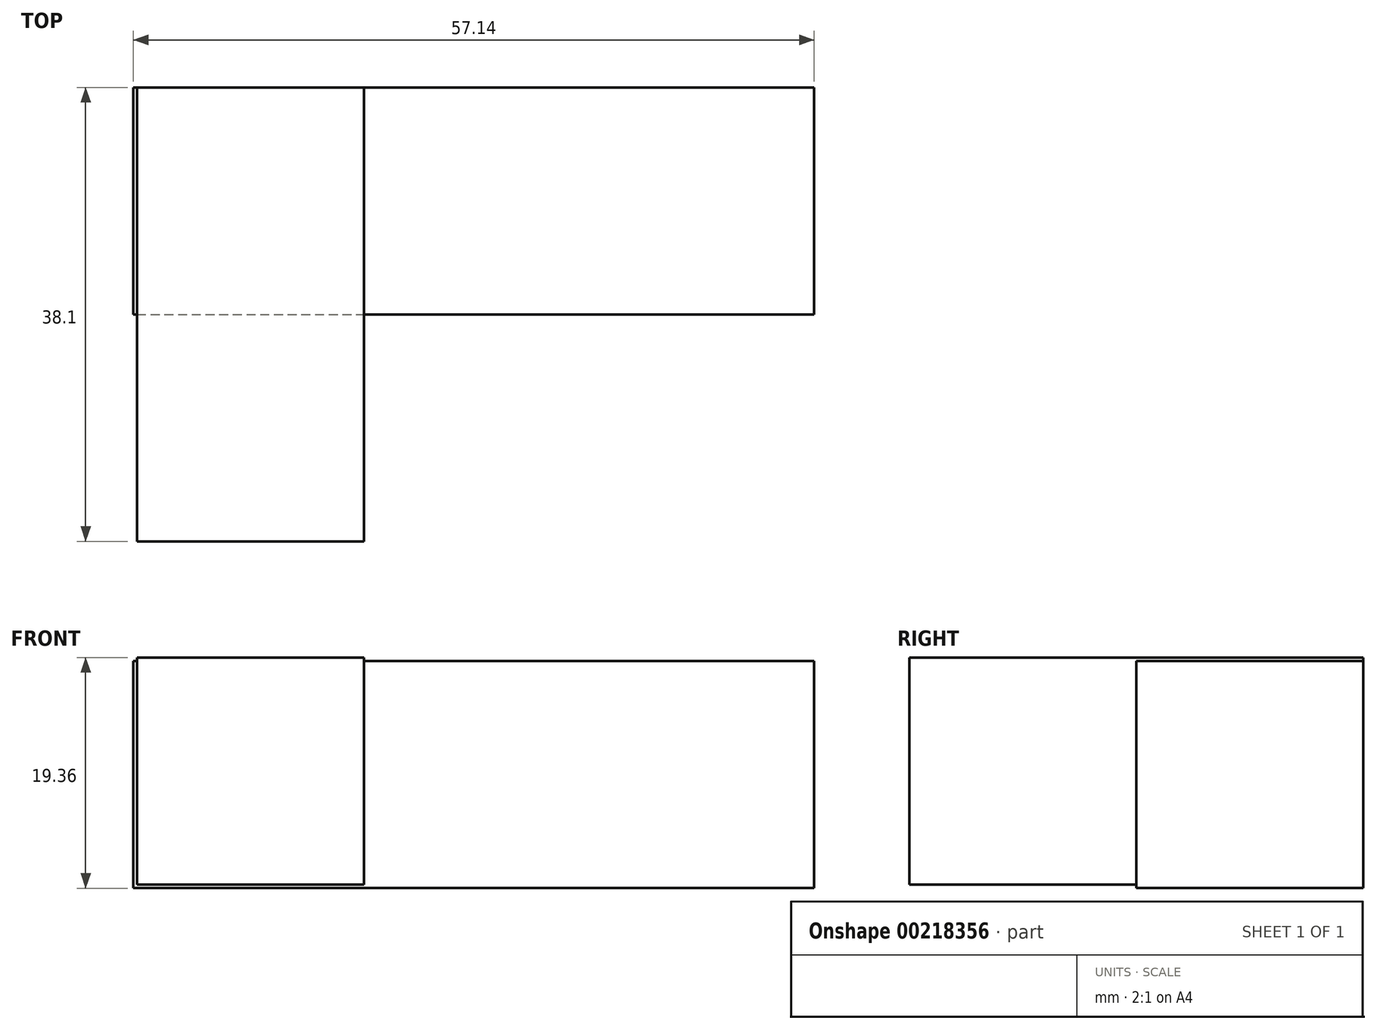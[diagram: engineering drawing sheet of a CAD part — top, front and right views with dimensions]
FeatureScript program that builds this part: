
annotation { "Feature Type Name" : "Feature", "Feature Type Description" : "" }
export const myFeature = defineFeature(function(context is Context, id is Id, definition is map)
    precondition{}
    {
        {
            var Q0;
            Q0=qCreatedBy(makeId("Front.planeOp"),FACE);
            var sketch = newSketch(context, id + "F0", { "sketchPlane" : qUnion([Q0])});
            skLineSegment(sketch, "E0.bottom", {"start": v(28.58, 9.53) * mm, "end": v(-28.58, 9.53) * mm});
            skLineSegment(sketch, "E0.top", {"start": v(28.58, -9.53) * mm, "end": v(-28.58, -9.53) * mm});
            skLineSegment(sketch, "E0.left", {"start": v(28.58, 9.53) * mm, "end": v(28.58, -9.53) * mm});
            skLineSegment(sketch, "E0.right", {"start": v(-28.58, 9.53) * mm, "end": v(-28.58, -9.53) * mm});
            skPoint(sketch, "E0.middle", {"position": v(0, 0) * mm});
            skLineSegment(sketch, "E1.bottom", {"start": v(-28.58, -9.53) * mm, "end": v(-9.53, -9.53) * mm});
            skLineSegment(sketch, "E1.top", {"start": v(-28.57, -47.62) * mm, "end": v(-9.52, -47.62) * mm});
            skLineSegment(sketch, "E1.left", {"start": v(-28.58, -9.53) * mm, "end": v(-28.58, -47.62) * mm});
            skLineSegment(sketch, "E1.right", {"start": v(-9.53, -9.52) * mm, "end": v(-9.52, -47.62) * mm});
            skSolve(sketch);
        }
        {
            var Q0;
            Q0=makeQuery(id+"F0.imprint","IMPRINT",FACE,{"disambiguationData":[TD([[makeQuery(id+"F0.imprint","IMPRINT",EDGE,{"derivedFrom":sQuery(id+"F0.wireOp",EDGE,"E0.bottom")}),1.0]])]});
            var sketch = newSketch(context, id + "F1", { "sketchPlane" : qUnion([Q0])});
            skLineSegment(sketch, "E2.bottom", {"start": v(-28.27, 9.83) * mm, "end": v(-9.22, 9.83) * mm});
            skLineSegment(sketch, "E2.top", {"start": v(-28.27, -9.22) * mm, "end": v(-9.22, -9.22) * mm});
            skLineSegment(sketch, "E2.left", {"start": v(-28.27, 9.83) * mm, "end": v(-28.27, -9.22) * mm});
            skLineSegment(sketch, "E2.right", {"start": v(-9.22, 9.83) * mm, "end": v(-9.22, -9.22) * mm});
            skSolve(sketch);
        }
        {
            var Q0;
            Q0 = qSketchRegion(id + "F1", true);
            extrude(context, id + "F2", {"entities" : qUnion([Q0]), "depth" : 38.1 * mm});
        }
        {
            var Q0;
            Q0=makeQuery(id+"F0.imprint","IMPRINT",FACE,{"disambiguationData":[TD([[makeQuery(id+"F0.imprint","IMPRINT",EDGE,{"derivedFrom":sQuery(id+"F0.wireOp",EDGE,"E0.bottom")}),1.0]])]});
            var Q1;
            Q1=makeQuery(id+"F0.imprint","IMPRINT",FACE,{"disambiguationData":[TD([[makeQuery(id+"F0.imprint","IMPRINT",EDGE,{"derivedFrom":sQuery(id+"F0.wireOp",EDGE,"E1.bottom")}),-1.0]])]});
            extrude(context, id + "F3", {"entities" : qUnion([Q0, Q1]), "operationType" : NewBodyOperationType.ADD, "depth" : 19.05 * mm});
        }
    });
